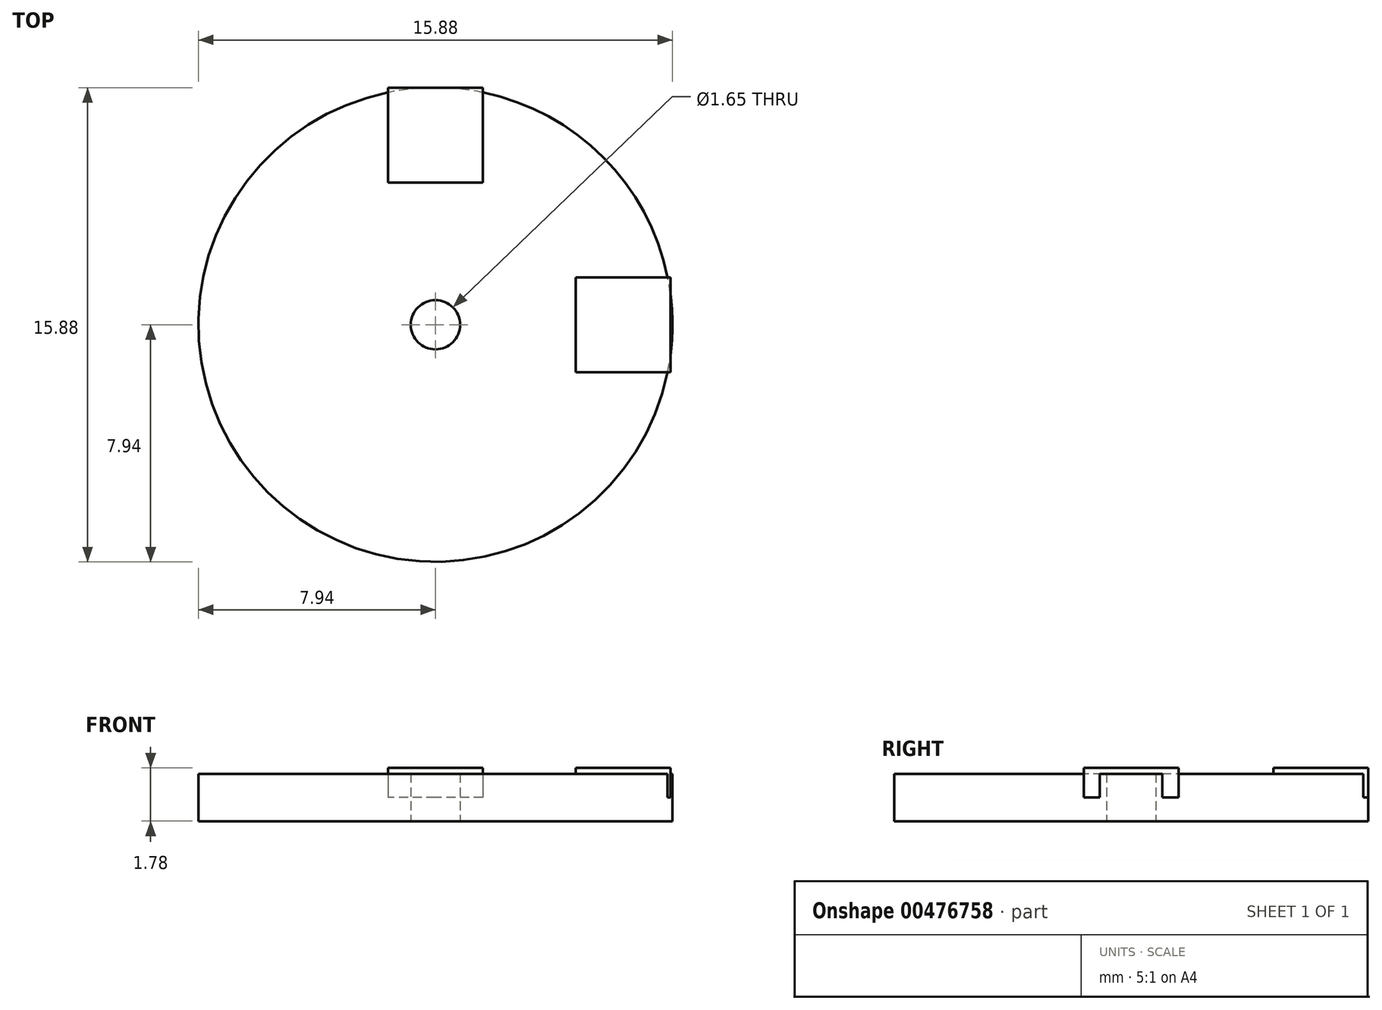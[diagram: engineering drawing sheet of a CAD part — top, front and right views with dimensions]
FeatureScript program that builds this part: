
annotation { "Feature Type Name" : "Feature", "Feature Type Description" : "" }
export const myFeature = defineFeature(function(context is Context, id is Id, definition is map)
    precondition{}
    {
        {
            var Q0;
            Q0=qCreatedBy(makeId("Top.planeOp"),FACE);
            var sketch = newSketch(context, id + "F0", { "sketchPlane" : qUnion([Q0])});
            skCircle(sketch, "E0", {"center": v(0, 0) * mm, "radius": 7.94 * mm});
            skCircle(sketch, "E1", {"center": v(0, 0) * mm, "radius": 0.83 * mm});
            skSolve(sketch);
        }
        {
            var Q0;
            Q0=makeQuery(id+"F0.imprint","IMPRINT",FACE,{"disambiguationData":[TD([[makeQuery(id+"F0.imprint","IMPRINT",EDGE,{"derivedFrom":sQuery(id+"F0.wireOp",EDGE,"E0")}),1.0]])]});
            extrude(context, id + "F1", {"entities" : qUnion([Q0]), "depth" : 1.59 * mm, "symmetric" : true});
        }
        {
            var Q0;
            Q0=qCreatedBy(makeId("Top.planeOp"),FACE);
            var sketch = newSketch(context, id + "F2", { "sketchPlane" : qUnion([Q0])});
            skLineSegment(sketch, "E2.bottom", {"start": v(1.59, 4.76) * mm, "end": v(-1.59, 4.76) * mm});
            skLineSegment(sketch, "E2.top", {"start": v(1.59, 7.94) * mm, "end": v(-1.59, 7.94) * mm});
            skLineSegment(sketch, "E2.left", {"start": v(1.59, 4.76) * mm, "end": v(1.59, 7.94) * mm});
            skLineSegment(sketch, "E2.right", {"start": v(-1.59, 4.76) * mm, "end": v(-1.59, 7.94) * mm});
            skPoint(sketch, "E2.middle", {"position": v(0, 6.35) * mm});
            skSolve(sketch);
        }
        {
            var Q0;
            Q0=makeQuery(id+"F2.imprint","IMPRINT",FACE,{"disambiguationData":[TD([[makeQuery(id+"F2.imprint","IMPRINT",EDGE,{"derivedFrom":sQuery(id+"F2.wireOp",EDGE,"E2.bottom")}),-1.0]])]});
            extrude(context, id + "F3", {"entities" : qUnion([Q0]), "operationType" : NewBodyOperationType.ADD, "depth" : 0.99 * mm});
        }
        {
            var Q0;
            Q0=qCreatedBy(makeId("Top.planeOp"),FACE);
            var sketch = newSketch(context, id + "F4", { "sketchPlane" : qUnion([Q0])});
            skLineSegment(sketch, "E3.bottom", {"start": v(7.87, 1.59) * mm, "end": v(4.7, 1.59) * mm});
            skLineSegment(sketch, "E3.top", {"start": v(7.87, -1.59) * mm, "end": v(4.7, -1.59) * mm});
            skLineSegment(sketch, "E3.left", {"start": v(7.87, 1.59) * mm, "end": v(7.87, -1.59) * mm});
            skLineSegment(sketch, "E3.right", {"start": v(4.7, 1.59) * mm, "end": v(4.7, -1.59) * mm});
            skPoint(sketch, "E3.middle", {"position": v(6.28, 0) * mm});
            skLineSegment(sketch, "E4", {"start": v(-17.04, 0) * mm, "end": v(25.38, 0) * mm, "construction": true});
            skSolve(sketch);
        }
        {
            var Q0;
            Q0=makeQuery(id+"F4.imprint","IMPRINT",FACE,{"disambiguationData":[TD([[makeQuery(id+"F4.imprint","IMPRINT",EDGE,{"derivedFrom":sQuery(id+"F4.wireOp",EDGE,"E3.bottom")}),1.0]])]});
            extrude(context, id + "F5", {"entities" : qUnion([Q0]), "operationType" : NewBodyOperationType.ADD, "depth" : 0.99 * mm});
        }
    });
